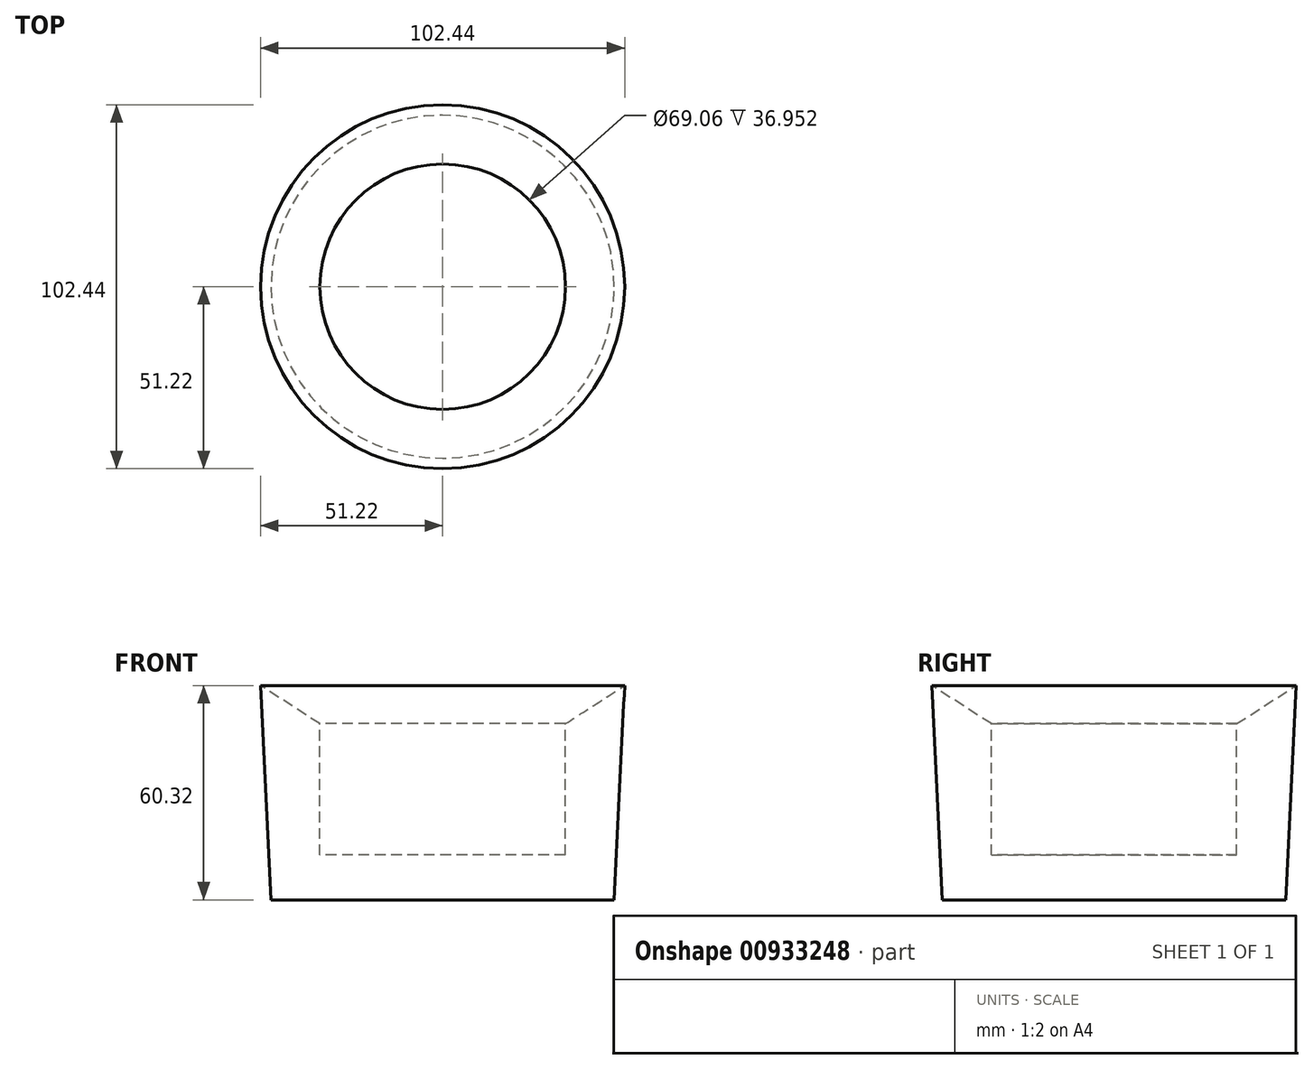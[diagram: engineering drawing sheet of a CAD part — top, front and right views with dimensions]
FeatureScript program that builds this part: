
annotation { "Feature Type Name" : "Feature", "Feature Type Description" : "" }
export const myFeature = defineFeature(function(context is Context, id is Id, definition is map)
    precondition{}
    {
        {
            var Q0;
            Q0=qCreatedBy(makeId("Front.planeOp"),FACE);
            var sketch = newSketch(context, id + "F0", { "sketchPlane" : qUnion([Q0])});
            skLineSegment(sketch, "E0", {"start": v(-46.37, 44.6) * mm, "end": v(-34.53, 36.95) * mm});
            skLineSegment(sketch, "E1", {"start": v(-34.53, 36.95) * mm, "end": v(-34.53, 0) * mm});
            skLineSegment(sketch, "E2", {"start": v(-34.53, 0) * mm, "end": v(0, 0) * mm});
            skLineSegment(sketch, "E3", {"start": v(0, 0) * mm, "end": v(0, -12.6) * mm});
            skLineSegment(sketch, "E4", {"start": v(0, -12.6) * mm, "end": v(-48.27, -12.6) * mm});
            skLineSegment(sketch, "E5", {"start": v(-46.37, 44.6) * mm, "end": v(-51.22, 47.72) * mm});
            skLineSegment(sketch, "E6", {"start": v(-51.22, 47.72) * mm, "end": v(-48.27, -12.6) * mm});
            skSolve(sketch);
        }
        {
            var Q0;
            Q0=makeQuery(id+"F0.imprint","IMPRINT",FACE,{"disambiguationData":[TD([[makeQuery(id+"F0.imprint","IMPRINT",EDGE,{"derivedFrom":sQuery(id+"F0.wireOp",EDGE,"E0")}),-1.0]])]});
            var Q1;
            Q1=sQuery(id+"F0.wireOp",EDGE,"E3");
            revolve(context, id + "F1", {"surfaceOperationType" : NewSurfaceOperationType.NEW, "entities" : qUnion([Q0]), "axis" : qUnion([Q1]), "revolveType" : RevolveType.FULL});
        }
    });
